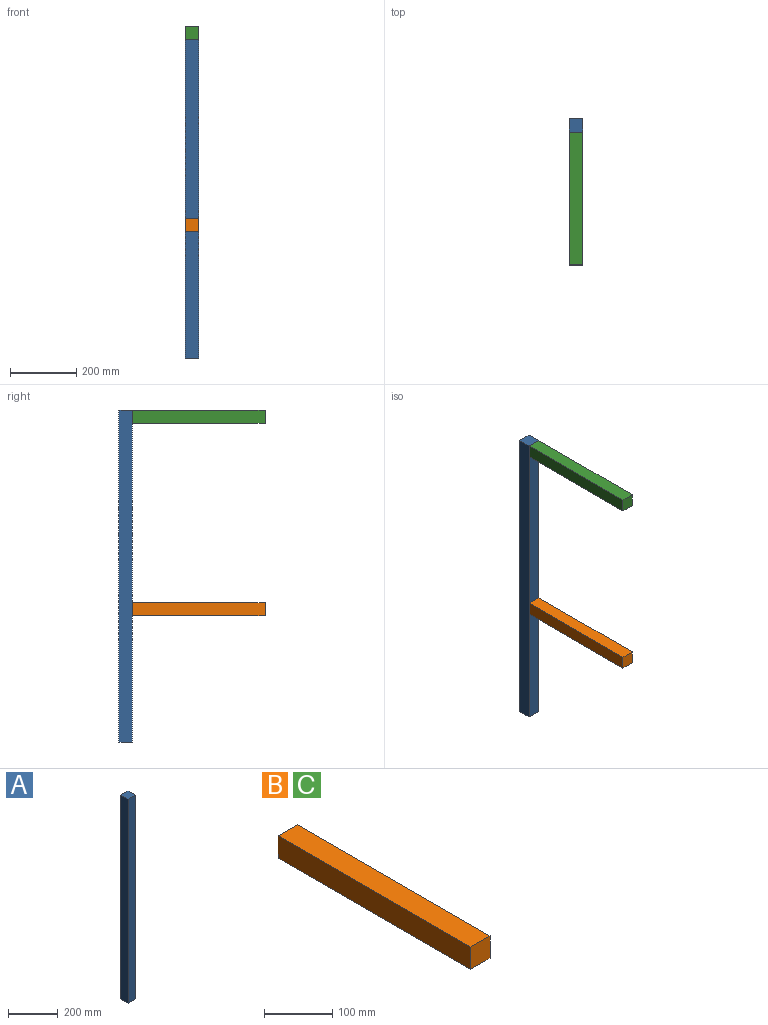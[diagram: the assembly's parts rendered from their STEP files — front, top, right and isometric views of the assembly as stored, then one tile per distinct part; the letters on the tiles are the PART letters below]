
ASSEMBLY  parts=3 mates=2
PART A: 6 faces, bbox 40x40x1000 mm
  f0: plane 1000x40mm, normal (0,1,0), area 40000mm2, adj f1,f3,f4,f5
  f1: plane 1000x40mm, normal (-1,0,0), area 40000mm2, adj f0,f2,f4,f5
  f2: plane 1000x40mm, normal (0,-1,0), area 40000mm2, adj f1,f3,f4,f5
  f3: plane 1000x40mm, normal (1,0,0), area 40000mm2, adj f0,f2,f4,f5
  f4: plane 40x40mm, normal (0,0,1), area 1600mm2, adj f0,f1,f2,f3
  f5: plane 40x40mm, normal (0,0,-1), area 1600mm2, adj f0,f1,f2,f3
PART B: 6 faces, bbox 40x400x40 mm
  f0: plane 400x40mm, normal (0,0,1), area 16000mm2, adj f1,f3,f4,f5
  f1: plane 400x40mm, normal (-1,0,0), area 16000mm2, adj f0,f2,f4,f5
  f2: plane 400x40mm, normal (0,0,-1), area 16000mm2, adj f1,f3,f4,f5
  f3: plane 400x40mm, normal (1,0,0), area 16000mm2, adj f0,f2,f4,f5
  f4: plane 40x40mm, normal (0,-1,0), area 1600mm2, adj f0,f1,f2,f3
  f5: plane 40x40mm, normal (0,1,0), area 1600mm2, adj f0,f1,f2,f3
PART C: same geometry as B
PLACE A t=(-548.99,191.45,-52.36)mm
PLACE B rot(axis=(1,0,0),180deg) t=(-71.69,-213.75,325.05)mm
PLACE C rot(axis=(1,0,0),180deg) t=(-71.69,-213.75,905.05)mm
MATE fastened C.f4 <-> A.f2  axis (0,1,0) through (-587.06,186.25,927.64)mm
MATE fastened B.f4 <-> A.f2  axis (0,1,0) through (-587.06,186.25,347.64)mm
